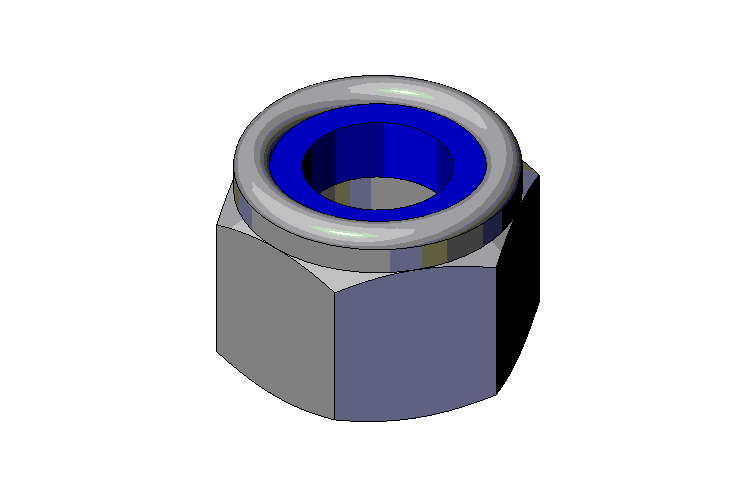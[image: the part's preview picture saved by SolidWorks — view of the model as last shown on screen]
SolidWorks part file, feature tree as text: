
SOLIDWORKS PART (.sldprt)
format: sldprt  version: not decoded by parser v0  size: 344,576 bytes
history: native  units: mm
features: plane x3, sketch x3, revolve x2, material x1, cut_extrude x1 (+10 scaffold rows collapsed)
feature tree (20):
  scaffold x10  (default folders/planes/origin — collapsed)
  material  "Matériau <non spécifié>"
  plane  "Face"
  plane  "Dessus"
  plane  "Droite"
  sketch  "Esquisse1"  dims[c1.D2=0.5mm c1.D10=~0.498816mm c1.D7=0.5mm c2.D10=0.5mm c2.D9=0.5mm c2.Rn=5.0mm c2.Hauteur=4.3mm c2.D1=~1.607849mm c3.D1=45.0deg c3.Pas=1.35mm c3.D3=~1.73058mm c4.D3=45.0deg c4.D4=~3.826341mm c5.D4=30.0deg c5.D2=30.0deg c5.D5=3.0mm c6.D5=30.0deg c6.D2=8.0mm c6.D4=4.0mm c7.D2=~3.826341mm c8.D2=150.0deg c9.D2=~11.474329mm c9.D1=~5.656854mm c9.Diamètre fileté=10.0mm c9.Cote sur plat=16.0mm c9.D6=1.5mm c9.Hf=11.4mm c9.Pas=1.5mm c9.Cote sur plats=16.0mm c9.Diamètre nominal=3.0mm c9.D7=3.0mm c9.D3=1.5mm c10.Diamètre nominal=10.0mm c10.D3=8.0mm c10.D7=~1.279273mm c11.D7=30.0deg c11.Hauteur=12.4mm c11.D8=~0.71951mm c12.D8=15.0deg c12.D9=0.5mm c12.D11=8.4mm c12.D2=~3.535534mm c13.D2=30.0deg c13.D10=~0.788459mm c13.D7=0.25mm c13.D9=0.5mm c14.D7=1.5mm c14.D9=0.75mm c14.D6=5.0mm c15.D7=6.0mm c15.D6=5.0mm c15.D2=~3.826341mm c16.D2=60.0deg c16.D3=~2.070552mm c17.D3=105.0deg c17.D6=8.0mm c17.D8=5.0mm c18.D3=~4.075583mm c18.D5=~7.826574mm c19.D3=5.0mm c19.D5=8.0mm c20.D3=~2.958182mm c20.D5=~6.810756mm c20.D6=~6.810756mm c21.D3=2.5mm c21.D5=~4.064516mm c21.D6=~2.070552mm c22.D6=105.0deg c22.D7=3.0mm c23.D7=30.0deg c23.D2=~3.826341mm c24.D2=60.0deg c25.D2=8.0mm c26.D2=105.0deg c26.D6=~2.376708mm c27.D6=60.0deg c27.Hauteur=6.3mm c27.D9=3.0mm c27.Diamètre nominal=5.0mm c27.Cote sur plats=8.0mm]
  revolve  "Base-Révolution"  Angle=360deg
  sketch  "Esquisse2"  dims[c1.D1=3.2mm c2.D1=120.0deg c3.D1=~0.536656mm c4.D1=150.0deg c5.D1=~1.269442mm c6.D1=120.0deg c6.D2=~1.326184mm c7.D2=120.0deg c7.D3=~1.33161mm c8.D3=~142.185676deg c8.D4=~3.626986mm c8.D1=~4.930361mm c9.D1=30.0deg c9.D2=~3.349004mm c10.D2=30.0deg c10.D3=2.5mm c10.D1=8.0mm c11.D1=30.0deg c11.D2=~11.313708mm c12.D2=30.0deg]
  cut_extrude  "Enlèv. mat.-Extru.2"  [1 undecoded]
  sketch  "Esquisse4"  dims[D1=4.2mm]
  revolve  "Boss.-Révol.1"  Angle=360deg
decode coverage: 5 of 6 modeling features carry decoded parameters
note: ~ marks probable driven/reference dimensions
note: 1 parameter value undecoded
note: suppression state not decoded; provenance and decode notes live in map.json
